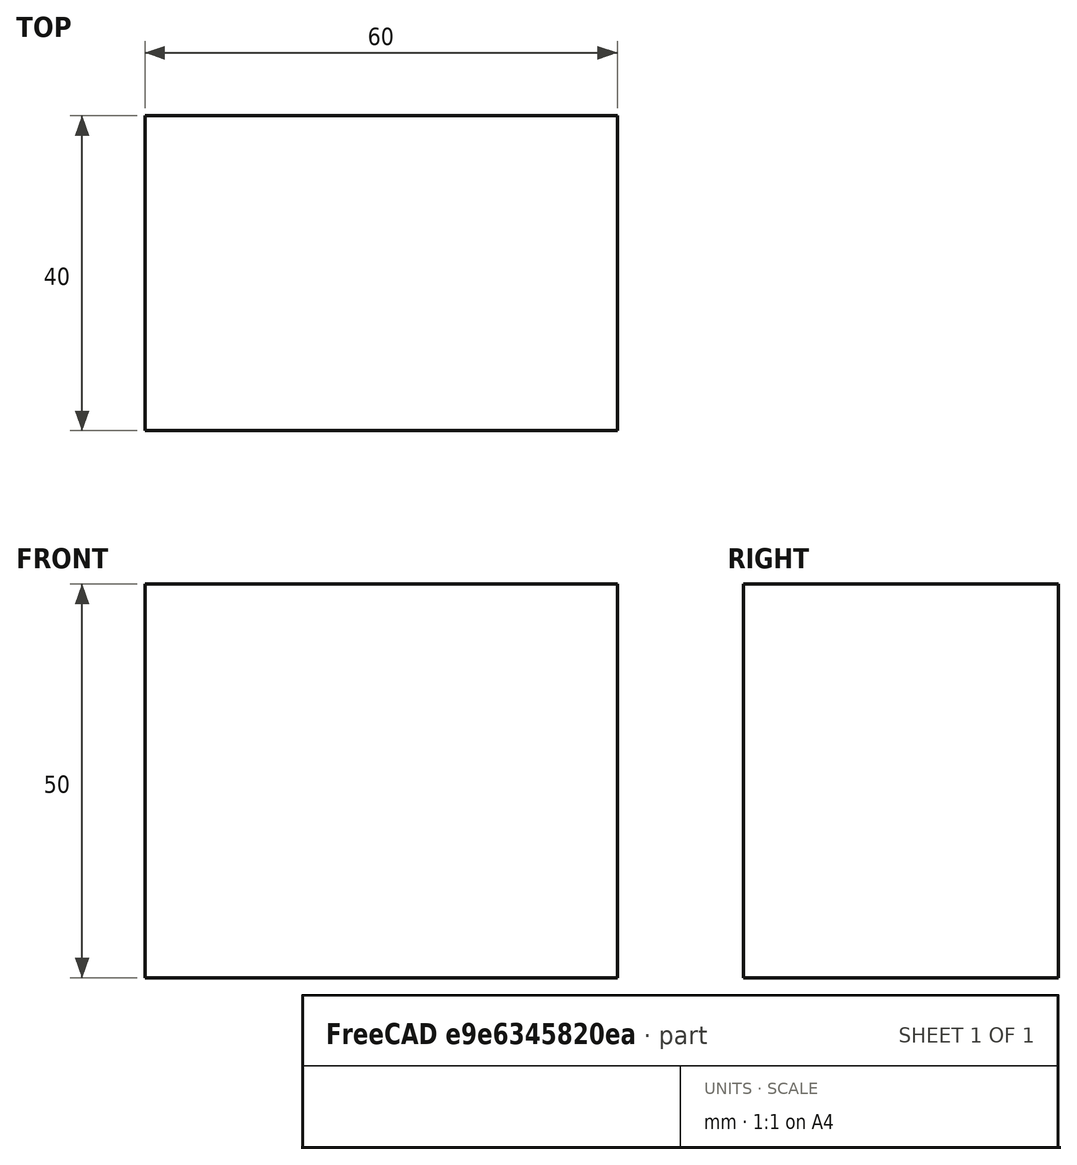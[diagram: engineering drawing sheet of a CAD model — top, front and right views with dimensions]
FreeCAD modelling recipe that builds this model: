
FCSTD DOCUMENT  (FreeCAD 0.15R4671 (Git))
Label: Flat Bar 60x40 EN10058 S235JR
License: All rights reserved
LicenseURL: http://en.wikipedia.org/wiki/All_rights_reserved
objects: Sketcher::SketchObject×1, Part::Extrusion×1
note: 2 computed .brp shape members not serialized (recipe doc carries the construction recipe); baked Part::Feature solids carry a one-line shape summary decoded from their .brp

FEATURE [Sketcher::SketchObject] Sketch
  sketch-geometry (4):
    g0: LineSegment StartX=-30 StartY=-20 StartZ=0 EndX=30 EndY=-20 EndZ=0
    g1: LineSegment StartX=30 StartY=-20 StartZ=0 EndX=30 EndY=20 EndZ=0
    g2: LineSegment StartX=30 StartY=20 StartZ=0 EndX=-30 EndY=20 EndZ=0
    g3: LineSegment StartX=-30 StartY=20 StartZ=0 EndX=-30 EndY=-20 EndZ=0
  constraints (12):
    c: Coincident(g0,g1)
    c: Coincident(g1,g2)
    c: Coincident(g2,g3)
    c: Coincident(g3,g0)
    c: Horizontal(g0)
    c: Horizontal(g2)
    c: Vertical(g1)
    c: Vertical(g3)
    c: Symmetric(g1,g2,g-2)
    c: Symmetric(g0,g1,g-1)
    c: DistanceY(g1) = 40
    c: DistanceX(g0) = 60
FEATURE [Part::Extrusion] Extrude  label="Flat Bar 60x40 EN10058 S235JR"
  Base = -> Sketch
  Dir = (0,0,50)
  Solid = true
